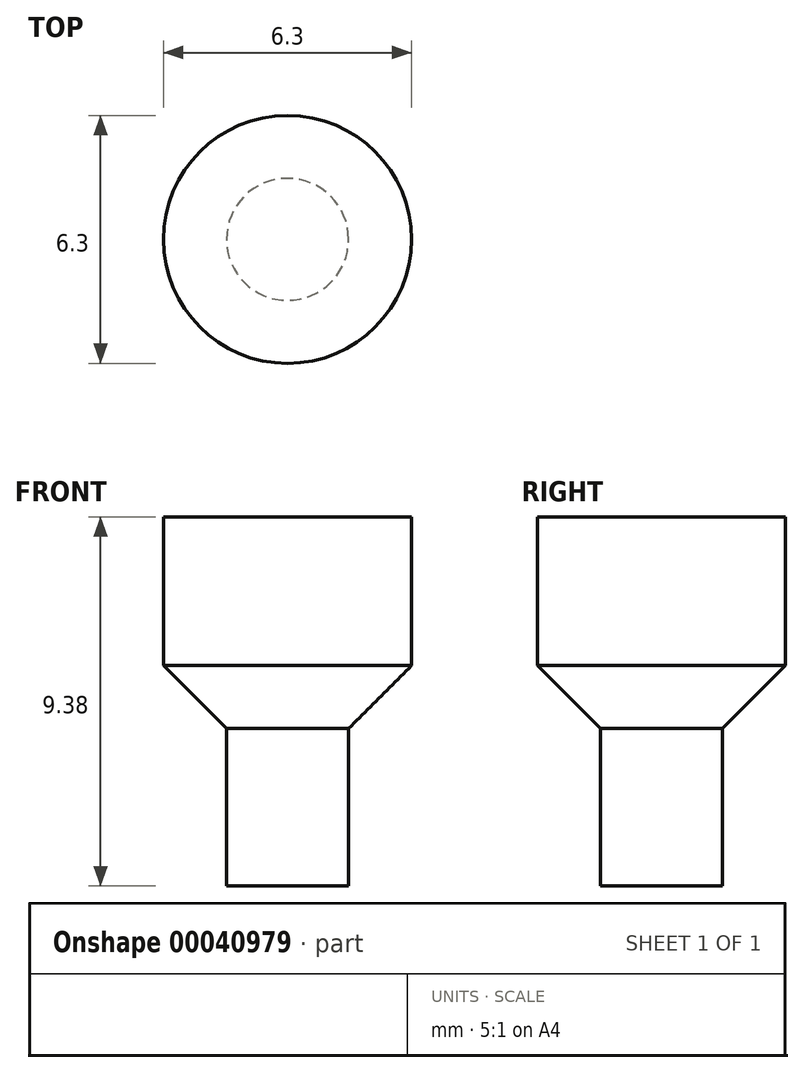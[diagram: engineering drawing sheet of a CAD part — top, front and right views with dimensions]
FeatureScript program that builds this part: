
annotation { "Feature Type Name" : "Feature", "Feature Type Description" : "" }
export const myFeature = defineFeature(function(context is Context, id is Id, definition is map)
    precondition{}
    {
        {
            var Q0;
            Q0=qCreatedBy(makeId("Right.planeOp"),FACE);
            var sketch = newSketch(context, id + "F0", { "sketchPlane" : qUnion([Q0])});
            skLineSegment(sketch, "E0", {"start": v(0, 3.78) * mm, "end": v(0, -5.6) * mm});
            skLineSegment(sketch, "E1", {"start": v(0, -5.6) * mm, "end": v(-1.5, -5.6) * mm});
            skLineSegment(sketch, "E2", {"start": v(-1.5, -5.6) * mm, "end": v(-1.5, -1.65) * mm, "construction": true});
            skLineSegment(sketch, "E3", {"start": v(-1.5, -1.65) * mm, "end": v(-3.15, -1.65) * mm, "construction": true});
            skLineSegment(sketch, "E4", {"start": v(-3.15, 3.78) * mm, "end": v(0, 3.78) * mm});
            skLineSegment(sketch, "E5", {"start": v(-1.5, -1.65) * mm, "end": v(-3.15, 0) * mm});
            skLineSegment(sketch, "E6", {"start": v(-3.15, 0) * mm, "end": v(0, 0) * mm});
            skLineSegment(sketch, "E7", {"start": v(-3.15, 3.78) * mm, "end": v(-3.15, 0) * mm});
            skLineSegment(sketch, "E8", {"start": v(-3.15, -1.65) * mm, "end": v(-3.15, 0) * mm, "construction": true});
            skLineSegment(sketch, "E9", {"start": v(-1.55, -5.6) * mm, "end": v(-1.55, -1.6) * mm});
            skLineSegment(sketch, "E10", {"start": v(0, -5.6) * mm, "end": v(-1.55, -5.6) * mm});
            skSolve(sketch);
        }
        {
            var Q0;
            Q0 = qSketchRegion(id + "F0", true);
            var Q1;
            Q1=sQuery(id+"F0.wireOp",EDGE,"E0");
            revolve(context, id + "F1", {"entities" : qUnion([Q0]), "axis" : qUnion([Q1]), "revolveType" : RevolveType.FULL});
        }
    });
